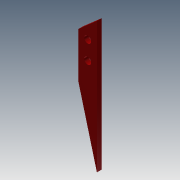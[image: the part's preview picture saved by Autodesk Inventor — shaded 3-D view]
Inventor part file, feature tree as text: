
AUTODESK INVENTOR PART (.ipt)
format: ipt  version: 2013 (Build 170138000, 138)  size: 82,432 bytes
history: native  units: mm
features: extrude x1, sketch x1
ambient origin geometry x8: Origin, YZ Plane, XZ Plane, XY Plane, X Axis, Y Axis, Z Axis, Center Point
bodies: Solid1 (feature_tree)
feature tree (2):
  extrude  "Extrusion1"  Depth=10.0mm
  sketch  "Sketch1"  dims[d2=27.0mm d9=10.0mm d10=3.0mm d13=20.0mm d16=8.0mm d17=3.0mm d18=2.0mm d19=0.0mm]
